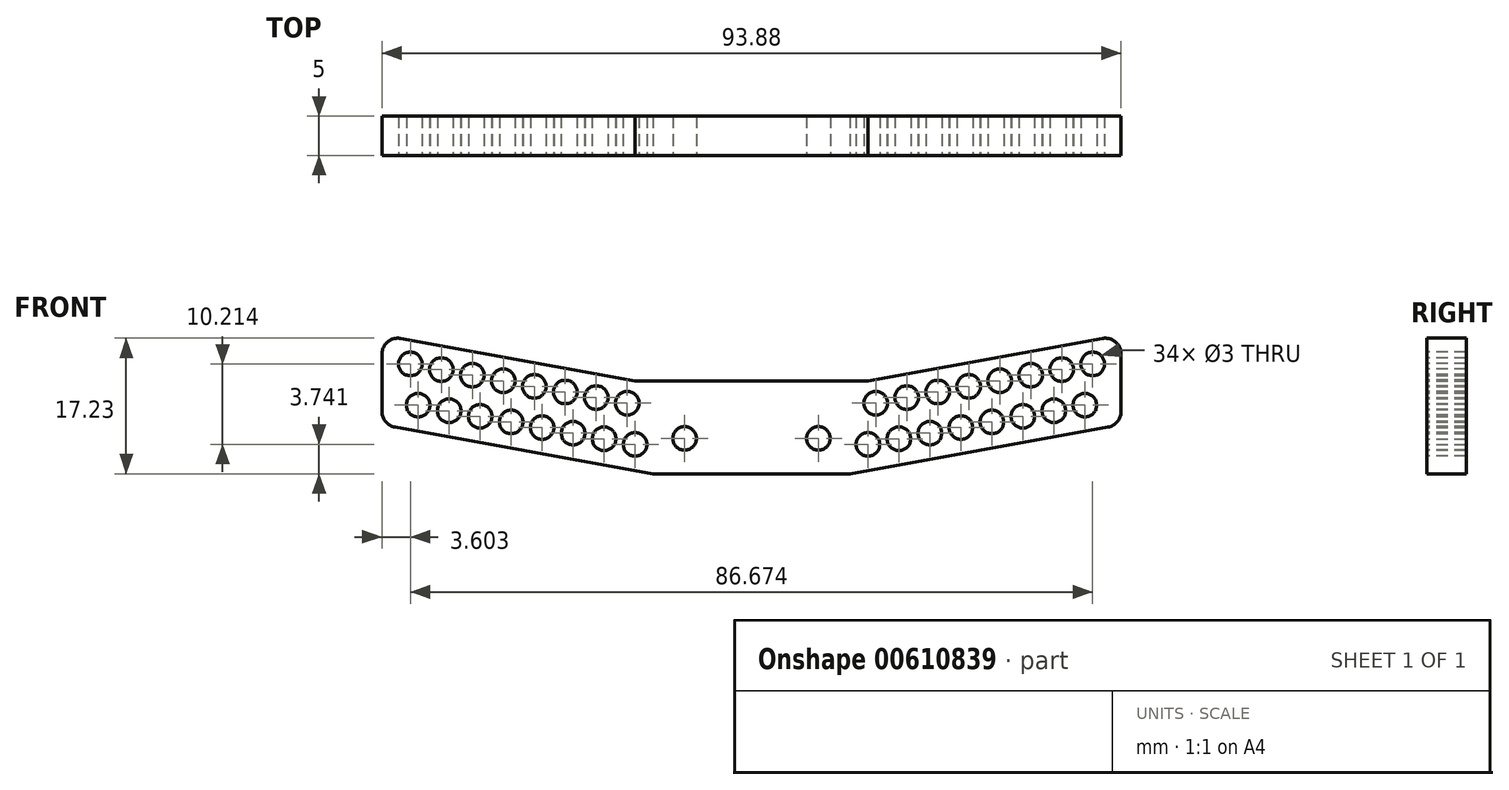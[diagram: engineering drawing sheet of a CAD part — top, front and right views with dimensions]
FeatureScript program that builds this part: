
annotation { "Feature Type Name" : "Feature", "Feature Type Description" : "" }
export const myFeature = defineFeature(function(context is Context, id is Id, definition is map)
    precondition{}
    {
        {
            var Q0;
            Q0=qCreatedBy(makeId("Front.planeOp"),FACE);
            var sketch = newSketch(context, id + "F0", { "sketchPlane" : qUnion([Q0])});
            skLineSegment(sketch, "E0", {"start": v(-46.94, 7.9) * mm, "end": v(-46.94, 15.23) * mm});
            skLineSegment(sketch, "E1", {"start": v(-45.3, 5.93) * mm, "end": v(-12.5, 0) * mm});
            skLineSegment(sketch, "E2", {"start": v(-12.5, 0) * mm, "end": v(0, 0) * mm});
            skLineSegment(sketch, "E3", {"start": v(0, 0) * mm, "end": v(0, 11.8) * mm});
            skLineSegment(sketch, "E4", {"start": v(0, 11.8) * mm, "end": v(-14.8, 11.8) * mm});
            skLineSegment(sketch, "E5", {"start": v(-44.58, 17.2) * mm, "end": v(-14.8, 11.8) * mm});
            skPoint(sketch, "E6.visualSharp", {"position": v(-46.94, 6.23) * mm});
            skArc(sketch, "E6.filletArc", {"start": v(-46.94, 7.9) * mm, "mid": v(-46.48, 6.62) * mm, "end": v(-45.3, 5.93) * mm});
            skPoint(sketch, "E7.newPointB", {"position": v(-50.3, 18.23) * mm});
            skArc(sketch, "E7.filletArc", {"start": v(-44.58, 17.2) * mm, "mid": v(-46.22, 16.76) * mm, "end": v(-46.94, 15.23) * mm});
            skCircle(sketch, "E8", {"center": v(-14.8, 3.74) * mm, "radius": 1.5 * mm});
            skCircle(sketch, "E9", {"center": v(-15.78, 8.97) * mm, "radius": 1.5 * mm});
            skCircle(sketch, "E10", {"center": v(-18.73, 4.45) * mm, "radius": 1.5 * mm});
            skCircle(sketch, "E11", {"center": v(-22.66, 5.16) * mm, "radius": 1.5 * mm});
            skCircle(sketch, "E12", {"center": v(-26.6, 5.88) * mm, "radius": 1.5 * mm});
            skCircle(sketch, "E13", {"center": v(-30.54, 6.59) * mm, "radius": 1.5 * mm});
            skCircle(sketch, "E14", {"center": v(-19.72, 9.68) * mm, "radius": 1.5 * mm});
            skCircle(sketch, "E15", {"center": v(-23.66, 10.4) * mm, "radius": 1.5 * mm});
            skCircle(sketch, "E16", {"center": v(-27.6, 11.1) * mm, "radius": 1.5 * mm});
            skCircle(sketch, "E17", {"center": v(-31.53, 11.82) * mm, "radius": 1.5 * mm});
            skCircle(sketch, "E18", {"center": v(-8.5, 4.5) * mm, "radius": 1.5 * mm});
            skCircle(sketch, "E19", {"center": v(-34.47, 7.3) * mm, "radius": 1.5 * mm});
            skCircle(sketch, "E20", {"center": v(-38.4, 8.01) * mm, "radius": 1.5 * mm});
            skCircle(sketch, "E21", {"center": v(-42.35, 8.72) * mm, "radius": 1.5 * mm});
            skCircle(sketch, "E22", {"center": v(-35.46, 12.53) * mm, "radius": 1.5 * mm});
            skCircle(sketch, "E23", {"center": v(-39.4, 13.24) * mm, "radius": 1.5 * mm});
            skCircle(sketch, "E24", {"center": v(-43.34, 13.95) * mm, "radius": 1.5 * mm});
            skArc(sketch, "E25.MirrorCS", {"start": v(46.94, 7.9) * mm, "mid": v(46.48, 6.62) * mm, "end": v(45.3, 5.93) * mm});
            skCircle(sketch, "E26.MirrorC", {"center": v(42.35, 8.72) * mm, "radius": 1.5 * mm});
            skCircle(sketch, "E27.MirrorC", {"center": v(31.53, 11.82) * mm, "radius": 1.5 * mm});
            skLineSegment(sketch, "E28.MirrorCS", {"start": v(12.5, 0) * mm, "end": v(0, 0) * mm});
            skCircle(sketch, "E29.MirrorC", {"center": v(23.66, 10.4) * mm, "radius": 1.5 * mm});
            skPoint(sketch, "E30.MirrorP", {"position": v(46.94, 6.23) * mm});
            skCircle(sketch, "E31.MirrorC", {"center": v(19.72, 9.68) * mm, "radius": 1.5 * mm});
            skCircle(sketch, "E32.MirrorC", {"center": v(43.34, 13.95) * mm, "radius": 1.5 * mm});
            skCircle(sketch, "E33.MirrorC", {"center": v(30.54, 6.59) * mm, "radius": 1.5 * mm});
            skCircle(sketch, "E34.MirrorC", {"center": v(35.46, 12.53) * mm, "radius": 1.5 * mm});
            skCircle(sketch, "E35.MirrorC", {"center": v(27.6, 11.1) * mm, "radius": 1.5 * mm});
            skCircle(sketch, "E36.MirrorC", {"center": v(39.4, 13.24) * mm, "radius": 1.5 * mm});
            skCircle(sketch, "E37.MirrorC", {"center": v(34.47, 7.3) * mm, "radius": 1.5 * mm});
            skCircle(sketch, "E38.MirrorC", {"center": v(38.4, 8.01) * mm, "radius": 1.5 * mm});
            skPoint(sketch, "E39.MirrorP", {"position": v(50.3, 18.23) * mm});
            skCircle(sketch, "E40.MirrorC", {"center": v(26.6, 5.88) * mm, "radius": 1.5 * mm});
            skCircle(sketch, "E41.MirrorC", {"center": v(22.66, 5.16) * mm, "radius": 1.5 * mm});
            skCircle(sketch, "E42.MirrorC", {"center": v(18.73, 4.45) * mm, "radius": 1.5 * mm});
            skLineSegment(sketch, "E43.MirrorCS", {"start": v(0, 11.8) * mm, "end": v(14.8, 11.8) * mm});
            skCircle(sketch, "E44.MirrorC", {"center": v(15.78, 8.97) * mm, "radius": 1.5 * mm});
            skLineSegment(sketch, "E45.MirrorCS", {"start": v(44.58, 17.2) * mm, "end": v(14.8, 11.8) * mm});
            skLineSegment(sketch, "E46.MirrorCS", {"start": v(45.3, 5.93) * mm, "end": v(12.5, 0) * mm});
            skCircle(sketch, "E47.MirrorC", {"center": v(8.5, 4.5) * mm, "radius": 1.5 * mm});
            skLineSegment(sketch, "E48.MirrorCS", {"start": v(46.94, 7.9) * mm, "end": v(46.94, 15.23) * mm});
            skCircle(sketch, "E49.MirrorC", {"center": v(14.8, 3.74) * mm, "radius": 1.5 * mm});
            skArc(sketch, "E50.MirrorCS", {"start": v(44.58, 17.2) * mm, "mid": v(46.22, 16.76) * mm, "end": v(46.94, 15.23) * mm});
            skSolve(sketch);
        }
        {
            var Q0;
            Q0 = qSketchRegion(id + "F0", true);
            extrude(context, id + "F1", {"entities" : qUnion([Q0]), "oppositeDirection" : true, "depth" : 5 * mm, "offsetDistance" : 25 * mm});
        }
    });
